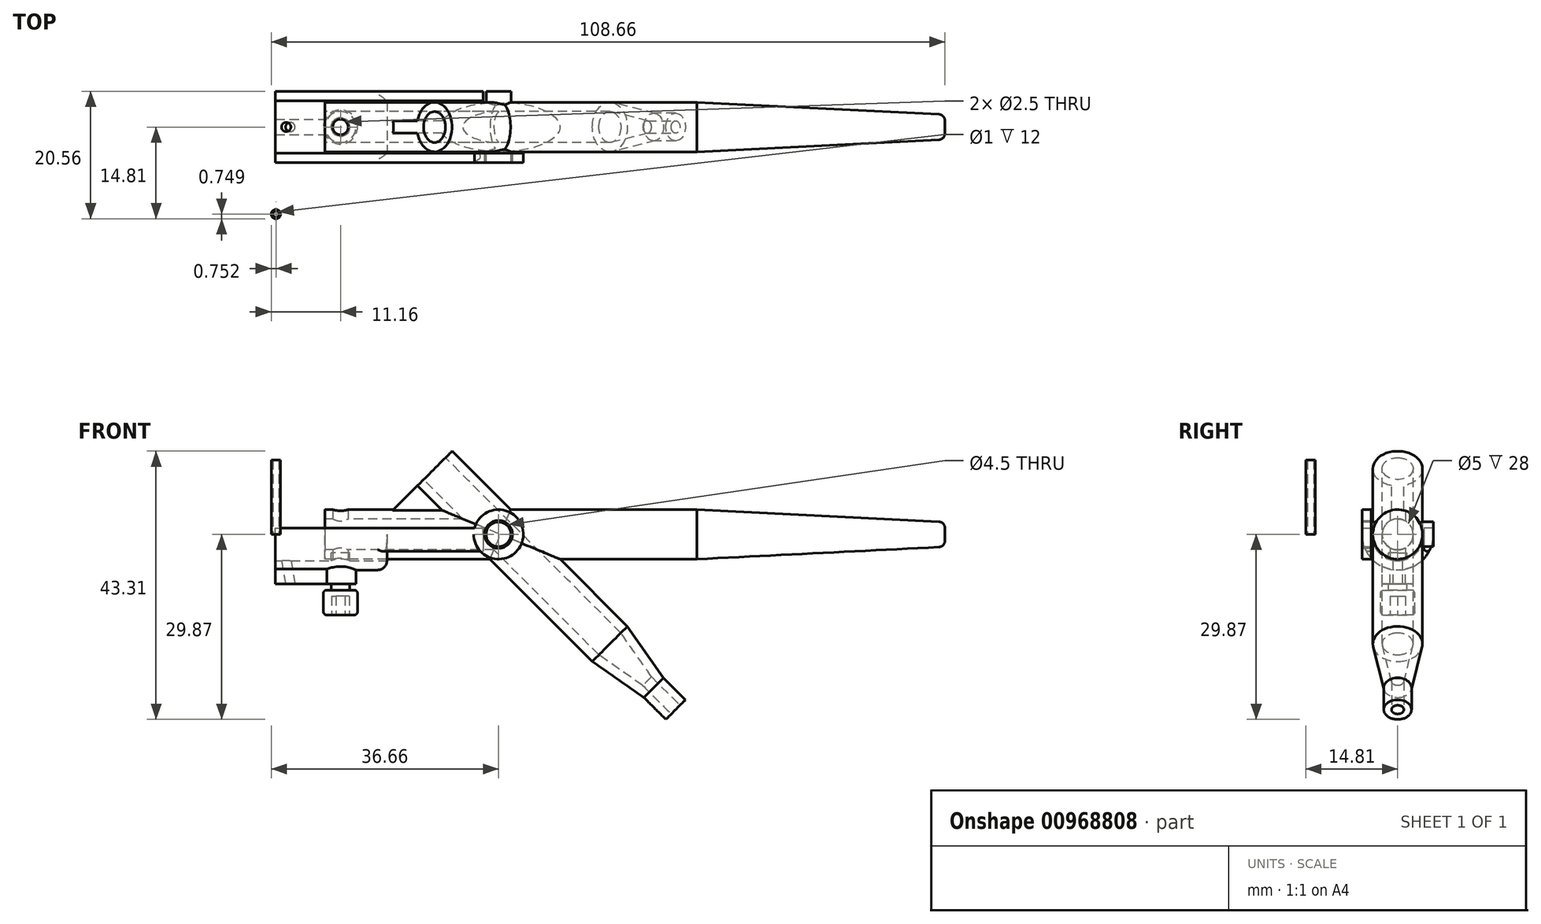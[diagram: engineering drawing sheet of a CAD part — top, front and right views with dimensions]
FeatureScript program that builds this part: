
annotation { "Feature Type Name" : "Feature", "Feature Type Description" : "" }
export const myFeature = defineFeature(function(context is Context, id is Id, definition is map)
    precondition{}
    {
        {
            var Q0;
            Q0=qCreatedBy(makeId("Right.planeOp"),FACE);
            var sketch = newSketch(context, id + "F0", { "sketchPlane" : qUnion([Q0])});
            skCircle(sketch, "E0", {"center": v(0, 0) * mm, "radius": 4 * mm});
            skSolve(sketch);
        }
        {
            var Q0;
            Q0=qSketchRegion(id+"F0",true);
            extrude(context, id + "F1", {"entities" : qUnion([Q0]), "depth" : 100 * mm});
        }
        {
            var Q0;
            Q0=makeQuery(id+"F1.opExtrude","CAP_EDGE",EDGE,{"disambiguationData":[OSD([sQuery(id+"F0.wireOp",EDGE,"E0")])],"isStart":false});
            chamfer(context, id + "F2", {"entities" : qUnion([Q0]), "chamferType" : ChamferType.TWO_OFFSETS, "width1" : 2 * mm, "oppositeDirection" : false, "width2" : 40 * mm, "tangentPropagation" : true});
        }
        {
            var Q0;
            Q0=makeQuery(id+"F1.opExtrude","CAP_FACE",FACE,{"disambiguationData":[OSD([sQuery(id+"F0.wireOp",EDGE,"E0")])],"isStart":true});
            var sketch = newSketch(context, id + "F3", { "sketchPlane" : qUnion([Q0])});
            skCircle(sketch, "E1", {"center": v(0, 0) * mm, "radius": 2.5 * mm});
            skSolve(sketch);
        }
        {
            var Q0;
            Q0=qCreatedBy(makeId("Top.planeOp"),FACE);
            var Q1;
            Q1=qCreatedBy(makeId("Right.planeOp"),FACE);
            cPlane(context, id + "F4", {"entities" : qUnion([Q0, Q1]), "cplaneType" : CPlaneType.MID_PLANE, "offset" : 25 * mm, "width" : 150 * mm, "height" : 150 * mm});
        }
        {
            var Q0;
            Q0=qCreatedBy(id+"F4.planeOp",FACE);
            var sketch = newSketch(context, id + "F5", { "sketchPlane" : qUnion([Q0])});
            skCircle(sketch, "E2", {"center": v(0, 20) * mm, "radius": 4 * mm});
            skSolve(sketch);
        }
        {
            var Q0;
            Q0=qSketchRegion(id+"F5",true);
            extrude(context, id + "F6", {"entities" : qUnion([Q0]), "operationType" : NewBodyOperationType.ADD, "oppositeDirection" : true, "depth" : 45 * mm, "hasSecondDirection" : true, "secondDirectionOppositeDirection" : true, "secondDirectionDepth" : 5 * mm});
        }
        {
            var Q0;
            Q0=makeQuery(id+"F6.opExtrude","CAP_FACE",FACE,{"disambiguationData":[OSD([sQuery(id+"F5.wireOp",EDGE,"E2")])],"isStart":true});
            var sketch = newSketch(context, id + "F7", { "sketchPlane" : qUnion([Q0])});
            skCircle(sketch, "E3", {"center": v(0, 20) * mm, "radius": 2.5 * mm});
            skSolve(sketch);
        }
        {
            var Q0;
            Q0=qCreatedBy(makeId("Front.planeOp"),FACE);
            var sketch = newSketch(context, id + "F8", { "sketchPlane" : qUnion([Q0])});
            skCircle(sketch, "E4", {"center": v(28, 0) * mm, "radius": 2 * mm});
            skSolve(sketch);
        }
        {
            var Q0;
            Q0=qSketchRegion(id+"F8",true);
            extrude(context, id + "F9", {"entities" : qUnion([Q0]), "operationType" : NewBodyOperationType.ADD, "endBound" : BoundingType.SYMMETRIC, "depth" : 11.5 * mm, "hasSecondDirection" : true, "secondDirectionOppositeDirection" : true, "secondDirectionDepth" : 25 * mm});
        }
        {
            var Q0;
            Q0=qSketchRegion(id+"F7",true);
            extrude(context, id + "F10", {"entities" : qUnion([Q0]), "operationType" : NewBodyOperationType.REMOVE, "endBound" : BoundingType.THROUGH_ALL, "oppositeDirection" : true, "depth" : 25 * mm});
        }
        {
            var Q0;
            Q0=makeQuery(id+"F6.opExtrude","CAP_FACE",FACE,{"disambiguationData":[OSD([sQuery(id+"F5.wireOp",EDGE,"E2")])],"isStart":false});
            var sketch = newSketch(context, id + "F11", { "sketchPlane" : qUnion([Q0])});
            skCircle(sketch, "E5.0", {"center": v(0, 20) * mm, "radius": 4 * mm});
            skSolve(sketch);
        }
        {
            var Q0;
            Q0=qSketchRegion(id+"F11",true);
            extrude(context, id + "F12", {"entities" : qUnion([Q0]), "operationType" : NewBodyOperationType.ADD, "depth" : 10 * mm, "hasDraft" : true, "draftAngle" : 10 * degree, "draftPullDirection" : true});
        }
        {
            var Q0;
            Q0=makeQuery(id+"F12.opExtrude","CAP_FACE",FACE,{"disambiguationData":[OSD([sQuery(id+"F11.wireOp",EDGE,"E5.0")])],"isStart":true});
            extrude(context, id + "F13", {"entities" : qUnion([Q0]), "operationType" : NewBodyOperationType.REMOVE, "oppositeDirection" : true, "depth" : 25 * mm, "hasDraft" : true, "draftAngle" : 10 * degree, "draftPullDirection" : true});
        }
        {
            var Q0;
            Q0=makeQuery(id+"F12.opExtrude","CAP_FACE",FACE,{"disambiguationData":[OSD([sQuery(id+"F11.wireOp",EDGE,"E5.0")])],"isStart":false});
            extrude(context, id + "F14", {"entities" : qUnion([Q0]), "operationType" : NewBodyOperationType.ADD, "depth" : 5 * mm});
        }
        {
            var Q0;
            Q0=makeQuery(id+"F14.opExtrude","CAP_FACE",FACE,{"disambiguationData":[OSD([sQuery(id+"F11.wireOp",EDGE,"E5.0")])],"isStart":false});
            var sketch = newSketch(context, id + "F15", { "sketchPlane" : qUnion([Q0])});
            skCircle(sketch, "E6", {"center": v(0, 20) * mm, "radius": 1 * mm});
            skSolve(sketch);
        }
        {
            var Q0;
            Q0=qSketchRegion(id+"F15",true);
            extrude(context, id + "F16", {"entities" : qUnion([Q0]), "operationType" : NewBodyOperationType.REMOVE, "endBound" : BoundingType.THROUGH_ALL, "oppositeDirection" : true, "depth" : 25 * mm});
        }
        {
            var Q0;
            Q0=makeQuery(id+"F6.opExtrude","CAP_FACE",FACE,{"disambiguationData":[OSD([sQuery(id+"F5.wireOp",EDGE,"E2")])],"isStart":true});
            var sketch = newSketch(context, id + "F17", { "sketchPlane" : qUnion([Q0])});
            skLineSegment(sketch, "E7.bottom", {"start": v(1, 10) * mm, "end": v(-1, 10) * mm});
            skLineSegment(sketch, "E7.top", {"start": v(1, 17) * mm, "end": v(-1, 17) * mm});
            skLineSegment(sketch, "E7.left", {"start": v(1, 10) * mm, "end": v(1, 17) * mm});
            skLineSegment(sketch, "E7.right", {"start": v(-1, 10) * mm, "end": v(-1, 17) * mm});
            skPoint(sketch, "E7.middle", {"position": v(0, 0) * mm});
            skSolve(sketch);
        }
        {
            var Q0;
            Q0=qSketchRegion(id+"F17",true);
            var Q1;
            {var subQ0=sQuery(id+"F0.wireOp",EDGE,"E0");var subQ1=makeQuery(id+"F1.opExtrude","SWEPT_FACE",FACE,{"disambiguationData":[OSD([subQ0])]});Q1=makeQuery(id+"F6.boolean.opBoolean","SPLIT",FACE,{"disambiguationData":[TD([makeQuery(id+"F1.opExtrude","CAP_FACE",FACE,{"disambiguationData":[OSD([subQ0])],"isStart":true})])],"derivedFrom":subQ1});}
            extrude(context, id + "F18", {"entities" : qUnion([Q0]), "operationType" : NewBodyOperationType.ADD, "oppositeDirection" : true, "endBoundEntityFace" : qUnion([Q1]), "depth" : 6 * mm});
        }
        {
            var Q0;
            Q0=qSketchRegion(id+"F3",true);
            extrude(context, id + "F19", {"entities" : qUnion([Q0]), "operationType" : NewBodyOperationType.REMOVE, "oppositeDirection" : true, "depth" : 28 * mm});
        }
        {
            var Q0;
            Q0=makeQuery(id+"F1.opExtrude","CAP_FACE",FACE,{"disambiguationData":[OSD([sQuery(id+"F0.wireOp",EDGE,"E0")])],"isStart":true});
            var sketch = newSketch(context, id + "F20", { "sketchPlane" : qUnion([Q0])});
            skArc(sketch, "E8", {"start": v(4.25, 0) * mm, "mid": v(0, -4.25) * mm, "end": v(-4.25, 0) * mm});
            skArc(sketch, "E9", {"start": v(5.75, 0) * mm, "mid": v(0, -5.75) * mm, "end": v(-5.75, 0) * mm});
            skLineSegment(sketch, "E10", {"start": v(-5.75, 0) * mm, "end": v(-5.75, 1) * mm});
            skLineSegment(sketch, "E11", {"start": v(-5.75, 1) * mm, "end": v(-4.25, 1) * mm});
            skLineSegment(sketch, "E12", {"start": v(-4.25, 1) * mm, "end": v(-4.25, 0) * mm});
            skLineSegment(sketch, "E13", {"start": v(4.25, 0) * mm, "end": v(4.25, 1) * mm});
            skLineSegment(sketch, "E14", {"start": v(4.25, 1) * mm, "end": v(5.75, 1) * mm});
            skLineSegment(sketch, "E15", {"start": v(5.75, 1) * mm, "end": v(5.75, 0) * mm});
            skSolve(sketch);
        }
        {
            var Q0;
            Q0=qSketchRegion(id+"F20",true);
            extrude(context, id + "F21", {"entities" : qUnion([Q0]), "depth" : 8 * mm, "hasSecondDirection" : true, "secondDirectionOppositeDirection" : true, "secondDirectionDepth" : 10 * mm});
        }
        {
            var Q0;
            Q0=makeQuery(id+"F21.opExtrude","CAP_FACE",FACE,{"disambiguationData":[OSD([sQuery(id+"F20.wireOp",EDGE,"E8"),sQuery(id+"F20.wireOp",EDGE,"E9"),sQuery(id+"F20.wireOp",EDGE,"E10"),sQuery(id+"F20.wireOp",EDGE,"E11"),sQuery(id+"F20.wireOp",EDGE,"E12"),sQuery(id+"F20.wireOp",EDGE,"E13"),sQuery(id+"F20.wireOp",EDGE,"E14"),sQuery(id+"F20.wireOp",EDGE,"E15")])],"isStart":true});
            var sketch = newSketch(context, id + "F22", { "sketchPlane" : qUnion([Q0])});
            skLineSegment(sketch, "E16", {"start": v(4.25, 1) * mm, "end": v(4.25, -3.87) * mm});
            skLineSegment(sketch, "E17", {"start": v(-4.25, 1) * mm, "end": v(-4.25, -3.87) * mm});
            skSolve(sketch);
        }
        {
            var Q0;
            {var subQ3=makeQuery(id+"F21.opExtrude","CAP_EDGE",EDGE,{"disambiguationData":[OSD([sQuery(id+"F20.wireOp",EDGE,"E10")])],"isStart":true});Q0=makeQuery(id+"F22.imprint","IMPRINT",FACE,{"disambiguationData":[TD([[makeQuery(id+"F22.imprint","IMPRINT",EDGE,{"derivedFrom":subQ3}),1.0]])]});}
            var Q1;
            {var subQ3=makeQuery(id+"F21.opExtrude","CAP_EDGE",EDGE,{"disambiguationData":[OSD([sQuery(id+"F20.wireOp",EDGE,"E14")])],"isStart":true});Q1=makeQuery(id+"F22.imprint","IMPRINT",FACE,{"disambiguationData":[TD([[makeQuery(id+"F22.imprint","IMPRINT",EDGE,{"derivedFrom":subQ3}),1.0]])]});}
            extrude(context, id + "F23", {"entities" : qUnion([Q0, Q1]), "operationType" : NewBodyOperationType.ADD, "depth" : 15.5 * mm});
        }
        {
            var Q0;
            Q0=makeQuery(id+"F21.opExtrude","CAP_EDGE",EDGE,{"disambiguationData":[OSD([sQuery(id+"F20.wireOp",EDGE,"E9")])],"isStart":true});
            fillet(context, id + "F24", {"entities" : qUnion([Q0]), "radius" : 1.5 * mm, "tangentPropagation" : true, "allowEdgeOverflow" : false});
        }
        {
            var Q0;
            Q0=makeQuery(id+"F23.opExtrude","SWEPT_EDGE",EDGE,{"disambiguationData":[OSD([sQuery(id+"F20.wireOp",EDGE,"E9"),sQuery(id+"F22.wireOp",EDGE,"E17")])]});
            var Q1;
            Q1=makeQuery(id+"F23.opExtrude","SWEPT_EDGE",EDGE,{"disambiguationData":[OSD([sQuery(id+"F20.wireOp",EDGE,"E9"),sQuery(id+"F22.wireOp",EDGE,"E16")])]});
            fillet(context, id + "F25", {"entities" : qUnion([Q0, Q1]), "radius" : 0.5 * mm, "tangentPropagation" : true, "allowEdgeOverflow" : false});
        }
        {
            var Q0;
            Q0=makeQuery(id+"F23.boolean.opBoolean","MERGE",FACE,{"derivedFrom":[makeQuery(id+"F21.opExtrude","SWEPT_FACE",FACE,{"disambiguationData":[OSD([sQuery(id+"F20.wireOp",EDGE,"E13")])]}),makeQuery(id+"F23.opExtrude","SWEPT_FACE",FACE,{"disambiguationData":[OSD([sQuery(id+"F22.wireOp",EDGE,"E17")])]})]});
            var sketch = newSketch(context, id + "F26", { "sketchPlane" : qUnion([Q0])});
            skCircle(sketch, "E18", {"center": v(-28, 0) * mm, "radius": 2.25 * mm});
            skCircle(sketch, "E19", {"center": v(-28, 0) * mm, "radius": 4 * mm});
            skSolve(sketch);
        }
        {
            var Q0;
            Q0=qSketchRegion(id+"F26",true);
            extrude(context, id + "F27", {"entities" : qUnion([Q0]), "operationType" : NewBodyOperationType.ADD, "oppositeDirection" : true, "depth" : 1.5 * mm});
        }
        {
            var Q0;
            Q0=qCreatedBy(makeId("Top.planeOp"),FACE);
            var sketch = newSketch(context, id + "F28", { "sketchPlane" : qUnion([Q0])});
            skCircle(sketch, "E20", {"center": v(2.5, 0) * mm, "radius": 2.5 * mm});
            skSolve(sketch);
        }
        {
            var Q0;
            Q0=qSketchRegion(id+"F28",true);
            extrude(context, id + "F29", {"entities" : qUnion([Q0]), "operationType" : NewBodyOperationType.ADD, "oppositeDirection" : true, "depth" : 8 * mm, "hasSecondDirection" : true, "secondDirectionOppositeDirection" : true, "secondDirectionDepth" : 5 * mm});
        }
        {
            var Q0;
            Q0=makeQuery(id+"F29.opExtrude","CAP_FACE",FACE,{"disambiguationData":[OSD([sQuery(id+"F28.wireOp",EDGE,"E20")])],"isStart":false});
            var sketch = newSketch(context, id + "F30", { "sketchPlane" : qUnion([Q0])});
            skCircle(sketch, "E21", {"center": v(2.5, 0) * mm, "radius": 1.25 * mm});
            skSolve(sketch);
        }
        {
            var Q0;
            Q0=qSketchRegion(id+"F30",true);
            extrude(context, id + "F31", {"entities" : qUnion([Q0]), "operationType" : NewBodyOperationType.REMOVE, "endBound" : BoundingType.THROUGH_ALL, "oppositeDirection" : true, "depth" : 25 * mm});
        }
        {
            var Q0;
            Q0=makeQuery(id+"F29.opExtrude","CAP_FACE",FACE,{"disambiguationData":[OSD([sQuery(id+"F28.wireOp",EDGE,"E20")])],"isStart":false});
            var sketch = newSketch(context, id + "F32", { "sketchPlane" : qUnion([Q0])});
            skCircle(sketch, "E22", {"center": v(2.5, 0) * mm, "radius": 1.5 * mm});
            skSolve(sketch);
        }
        {
            var Q0;
            Q0=qSketchRegion(id+"F32",true);
            extrude(context, id + "F33", {"entities" : qUnion([Q0]), "depth" : 1 * mm, "hasSecondDirection" : true, "secondDirectionOppositeDirection" : true, "secondDirectionDepth" : 5 * mm});
        }
        {
            var Q0;
            Q0=makeQuery(id+"F33.opExtrude","CAP_FACE",FACE,{"disambiguationData":[OSD([sQuery(id+"F32.wireOp",EDGE,"E22")])],"isStart":false});
            var sketch = newSketch(context, id + "F34", { "sketchPlane" : qUnion([Q0])});
            skCircle(sketch, "E23", {"center": v(2.5, 0) * mm, "radius": 2.75 * mm});
            skSolve(sketch);
        }
        {
            var Q0;
            Q0=qSketchRegion(id+"F34",true);
            extrude(context, id + "F35", {"entities" : qUnion([Q0]), "operationType" : NewBodyOperationType.ADD, "depth" : 4 * mm});
        }
        {
            var Q0;
            Q0=makeQuery(id+"F35.opExtrude","SWEPT_FACE",FACE,{"disambiguationData":[OSD([sQuery(id+"F34.wireOp",EDGE,"E23")])]});
            fillet(context, id + "F36", {"entities" : qUnion([Q0]), "radius" : .5 * mm, "tangentPropagation" : true, "allowEdgeOverflow" : false});
        }
        {
            var Q0;
            Q0=makeQuery(id+"F35.opExtrude","CAP_FACE",FACE,{"disambiguationData":[OSD([sQuery(id+"F34.wireOp",EDGE,"E23")])],"isStart":false});
            var sketch = newSketch(context, id + "F37", { "sketchPlane" : qUnion([Q0])});
            skCircle(sketch, "E24.cCircle", {"center": v(2.5, 0) * mm, "radius": 1.25 * mm, "construction": true});
            skLineSegment(sketch, "E24.0", {"start": v(3.22, -1.25) * mm, "end": v(1.78, -1.25) * mm});
            skLineSegment(sketch, "E24.1", {"start": v(1.78, -1.25) * mm, "end": v(1.06, 0) * mm});
            skLineSegment(sketch, "E24.2", {"start": v(1.06, 0) * mm, "end": v(1.78, 1.25) * mm});
            skLineSegment(sketch, "E24.3", {"start": v(1.78, 1.25) * mm, "end": v(3.22, 1.25) * mm});
            skLineSegment(sketch, "E24.4", {"start": v(3.22, 1.25) * mm, "end": v(3.94, 0) * mm});
            skLineSegment(sketch, "E24.5", {"start": v(3.94, 0) * mm, "end": v(3.22, -1.25) * mm});
            skPoint(sketch, "E24.0.midPoint", {"position": v(2.5, -1.25) * mm});
            skSolve(sketch);
        }
        {
            var Q0;
            Q0=makeQuery(id+"F21.opExtrude","CAP_FACE",FACE,{"disambiguationData":[OSD([sQuery(id+"F20.wireOp",EDGE,"E8"),sQuery(id+"F20.wireOp",EDGE,"E9"),sQuery(id+"F20.wireOp",EDGE,"E10"),sQuery(id+"F20.wireOp",EDGE,"E11"),sQuery(id+"F20.wireOp",EDGE,"E12"),sQuery(id+"F20.wireOp",EDGE,"E13"),sQuery(id+"F20.wireOp",EDGE,"E14"),sQuery(id+"F20.wireOp",EDGE,"E15")])],"isStart":false});
            var sketch = newSketch(context, id + "F38", { "sketchPlane" : qUnion([Q0])});
            skLineSegment(sketch, "E25.bottom", {"start": v(1.25, -8) * mm, "end": v(-1.25, -8) * mm});
            skLineSegment(sketch, "E25.top", {"start": v(1.25, -4.75) * mm, "end": v(-1.25, -4.75) * mm});
            skLineSegment(sketch, "E25.left", {"start": v(1.25, -8) * mm, "end": v(1.25, -4.75) * mm});
            skLineSegment(sketch, "E25.right", {"start": v(-1.25, -8) * mm, "end": v(-1.25, -4.75) * mm});
            skPoint(sketch, "E25.middle", {"position": v(0, -6.38) * mm});
            skPoint(sketch, "E25.centerSnap0", {"position": v(0, -5.75) * mm});
            skSolve(sketch);
        }
        {
            var Q0;
            Q0=qSketchRegion(id+"F38",true);
            extrude(context, id + "F39", {"entities" : qUnion([Q0]), "operationType" : NewBodyOperationType.ADD, "oppositeDirection" : true, "depth" : 9 * mm});
        }
        {
            var Q0;
            Q0=qSketchRegion(id+"F37",true);
            extrude(context, id + "F40", {"entities" : qUnion([Q0]), "operationType" : NewBodyOperationType.REMOVE, "oppositeDirection" : true, "depth" : 3 * mm});
        }
        {
            var Q0;
            Q0=qCreatedBy(makeId("Front.planeOp"),FACE);
            var sketch = newSketch(context, id + "F41", { "sketchPlane" : qUnion([Q0])});
            skLineSegment(sketch, "E26", {"start": v(0, 0) * mm, "end": v(-21, 0) * mm, "construction": true});
            skLineSegment(sketch, "E27.bottom", {"start": v(-7, 0) * mm, "end": v(-6.26, 0.13) * mm});
            skLineSegment(sketch, "E27.top", {"start": v(-5.18, -10.34) * mm, "end": v(-4.44, -10.2) * mm});
            skLineSegment(sketch, "E27.left", {"start": v(-7, 0) * mm, "end": v(-5.18, -10.34) * mm});
            skLineSegment(sketch, "E27.right", {"start": v(-6.26, 0.13) * mm, "end": v(-4.44, -10.2) * mm});
            skSolve(sketch);
        }
        {
            var Q0;
            Q0=qSketchRegion(id+"F41",true);
            var Q1;
            Q1=sQuery(id+"F41.wireOp",EDGE,"E27.left");
            revolve(context, id + "F42", {"operationType" : NewBodyOperationType.REMOVE, "entities" : qUnion([Q0]), "axis" : qUnion([Q1]), "revolveType" : RevolveType.FULL, "oppositeDirection" : true});
        }
        {
            var Q0;
            Q0=qCreatedBy(makeId("Top.planeOp"),FACE);
            var sketch = newSketch(context, id + "F43", { "sketchPlane" : qUnion([Q0])});
            skCircle(sketch, "E28", {"center": v(-7.9, -14.06) * mm, "radius": 0.75 * mm});
            skCircle(sketch, "E29", {"center": v(-7.9, -14.06) * mm, "radius": 0.5 * mm});
            skSolve(sketch);
        }
        {
            var Q0;
            Q0=qSketchRegion(id+"F43",true);
            extrude(context, id + "F44", {"entities" : qUnion([Q0]), "depth" : 12 * mm});
        }
        {
            var Q0;
            Q0=makeQuery(id+"F1.opExtrude","CAP_FACE",FACE,{"disambiguationData":[OSD([sQuery(id+"F0.wireOp",EDGE,"E0")])],"isStart":false});
            fillet(context, id + "F45", {"entities" : qUnion([Q0]), "radius" : 1 * mm, "tangentPropagation" : true, "allowEdgeOverflow" : false});
        }
    });
